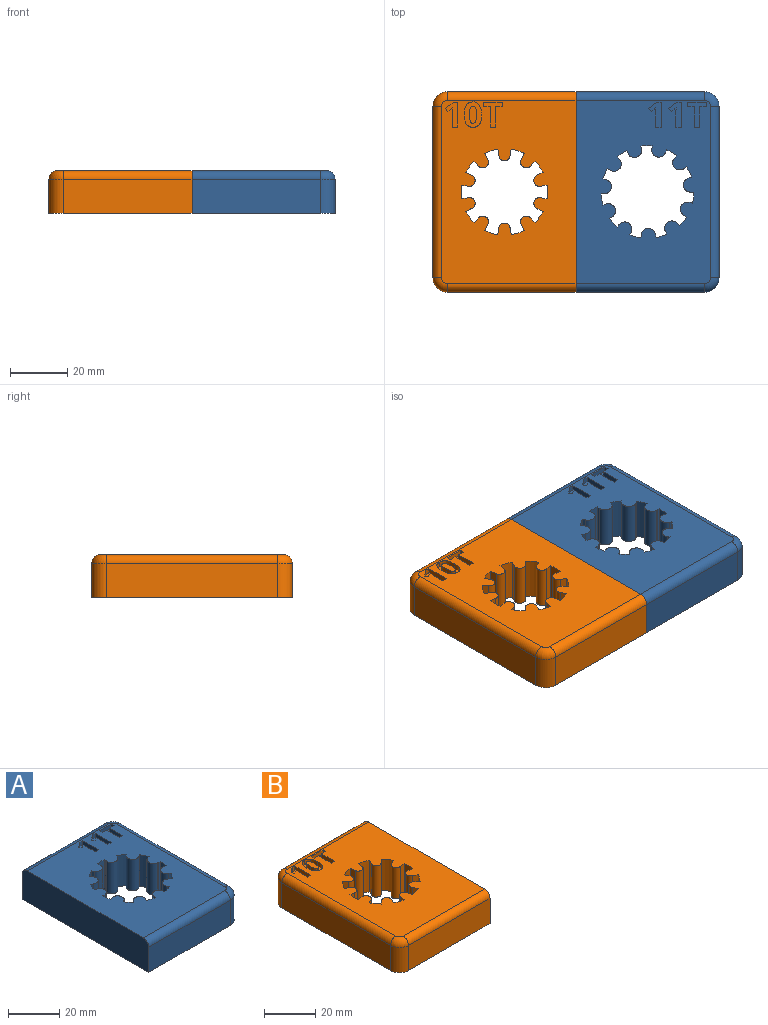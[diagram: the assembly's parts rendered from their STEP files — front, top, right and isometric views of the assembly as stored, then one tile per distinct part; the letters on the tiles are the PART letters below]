
ASSEMBLY  parts=2 mates=1
PART A: 101 faces, bbox 50x70x15 mm
  f0: plane 64x47mm, normal (0,0,1), area 2276.3mm2, adj f4,f6,f7,f8,f9,f10,f11,f12
  f1: plane 45x12mm, normal (0,-1,0), area 540mm2, adj f4,f5,f63,f69
  f2: plane 60x12mm, normal (1,0,0), area 720mm2, adj f5,f63,f64,f67
  f3: plane 45x12mm, normal (0,1,0), area 540mm2, adj f4,f5,f64,f65
  f4: plane 70x15mm, normal (-1,0,0), area 1046.1mm2, adj f0,f1,f3,f5,f65,f69
  f5: plane 70x50mm, normal (0,0,-1), area 2823.1mm2, adj f1,f2,f3,f4,f6,f7,f8,f9
  f6: cylinder r=16.23mm len=15mm, axis (0,0,1), area 59.6mm2, adj f0,f5,f7,f62
  f7: plane 15x0.99mm, normal (-0.99,0.12,0), area 15mm2, adj f0,f5,f6,f8
  f8: plane 15x0mm, normal (-0.1,-0.99,0), area 0.1mm2, adj f0,f5,f7,f9
  f9: plane 15x0.3mm, normal (-0.99,0.12,0), area 4.5mm2, adj f0,f5,f8,f10
  f10: cylinder r=2.5mm len=15mm, axis (0,0,1), area 102.6mm2, adj f0,f5,f9,f11
  f11: plane 15x1.2mm, normal (0.92,-0.4,0), area 19.5mm2, adj f0,f5,f10,f12
  f12: cylinder r=16.23mm len=15mm, axis (0,0,1), area 59.7mm2, adj f0,f5,f11,f13
  f13: plane 15x1mm, normal (-0.77,0.64,0), area 19.5mm2, adj f0,f5,f12,f14
  f14: cylinder r=2.5mm len=15mm, axis (0,0,1), area 102.6mm2, adj f0,f5,f13,f15
  f15: plane 15x1.08mm, normal (0.56,-0.83,0), area 19.5mm2, adj f0,f5,f14,f16
  f16: cylinder r=16.23mm len=15mm, axis (0,0,1), area 59.7mm2, adj f0,f5,f15,f17
  f17: plane 15x1.24mm, normal (-0.3,0.95,0), area 19.5mm2, adj f0,f5,f16,f18
  f18: cylinder r=2.5mm len=15mm, axis (0,0,1), area 102.5mm2, adj f0,f5,f17,f19
  f19: plane 15x0.31mm, normal (0.02,-1,0), area 4.6mm2, adj f0,f5,f18,f20
  f20: cylinder r=15.23mm len=15mm, axis (0,0,1), area 0.3mm2, adj f0,f5,f19,f21
  f21: plane 15x1mm, normal (0.02,-1,0), area 15mm2, adj f0,f5,f20,f22
  f22: cylinder r=16.23mm len=15mm, axis (0,0,1), area 59.3mm2, adj f0,f5,f21,f23
  f23: plane 15x1.26mm, normal (0.26,0.96,0), area 19.5mm2, adj f0,f5,f22,f24
  f24: cylinder r=2.5mm len=15mm, axis (0,0,1), area 107.1mm2, adj f0,f5,f23,f25
  f25: plane 15x0mm, normal (-0.84,0.54,0), area 0.1mm2, adj f0,f5,f24,f26
  f26: plane 15x0.85mm, normal (-0.52,-0.85,0), area 15mm2, adj f0,f5,f25,f27
  f27: cylinder r=16.23mm len=15mm, axis (0,0,1), area 59.5mm2, adj f0,f5,f26,f28
  f28: plane 15x0.74mm, normal (0.74,0.67,0), area 15mm2, adj f0,f5,f27,f29
  f29: plane 15x0mm, normal (-0.69,0.73,0), area 0.1mm2, adj f0,f5,f28,f30
  f30: cylinder r=2.5mm len=15mm, axis (0,0,1), area 111.6mm2, adj f0,f5,f29,f31
  f31: plane 15x0mm, normal (-0.41,0.91,0), area 0.1mm2, adj f0,f5,f30,f32
  f32: plane 15x0.9mm, normal (-0.9,-0.43,0), area 15mm2, adj f0,f5,f31,f33
  f33: cylinder r=16.23mm len=15mm, axis (0,0,1), area 59.5mm2, adj f0,f5,f32,f34
  f34: plane 15x0.99mm, normal (0.99,0.16,0), area 15mm2, adj f0,f5,f33,f35
  f35: plane 15x0mm, normal (-0.18,0.98,0), area 0.1mm2, adj f0,f5,f34,f36
  f36: cylinder r=2.5mm len=15mm, axis (0,0,1), area 107.1mm2, adj f0,f5,f35,f37
  f37: plane 15x1.29mm, normal (-0.99,0.12,0), area 19.5mm2, adj f0,f5,f36,f38
  f38: cylinder r=16.23mm len=15mm, axis (0,0,1), area 59.6mm2, adj f0,f5,f37,f39
  f39: plane 15x0.92mm, normal (0.92,-0.4,0), area 15mm2, adj f0,f5,f38,f40
  f40: plane 15x0mm, normal (0.38,0.93,0), area 0.1mm2, adj f0,f5,f39,f41
  f41: cylinder r=2.5mm len=15mm, axis (0,0,1), area 111.6mm2, adj f0,f5,f40,f42
  f42: plane 15x0mm, normal (0.66,0.75,0), area 0.1mm2, adj f0,f5,f41,f43
  f43: plane 15x0.77mm, normal (-0.77,0.64,0), area 15mm2, adj f0,f5,f42,f44
  f44: cylinder r=16.23mm len=15mm, axis (0,0,1), area 59.5mm2, adj f0,f5,f43,f45
  f45: plane 15x0.83mm, normal (0.56,-0.83,0), area 15mm2, adj f0,f5,f44,f46
  f46: plane 15x0mm, normal (0.82,0.58,0), area 0.1mm2, adj f0,f5,f45,f47
  f47: cylinder r=2.5mm len=15mm, axis (0,0,1), area 111.6mm2, adj f0,f5,f46,f48
  f48: plane 15x0mm, normal (0.96,0.28,0), area 0.1mm2, adj f0,f5,f47,f49
  f49: plane 15x0.95mm, normal (-0.3,0.95,0), area 15mm2, adj f0,f5,f48,f50
  f50: cylinder r=16.23mm len=15mm, axis (0,0,1), area 59.9mm2, adj f0,f5,f49,f51
  f51: plane 15x1.5mm, normal (0.02,-1,0), area 22.5mm2, adj f0,f5,f50,f52
  f52: cylinder r=2.5mm len=15mm, axis (0,0,1), area 104.2mm2, adj f0,f5,f51,f53
  f53: plane 15x0mm, normal (0.96,-0.28,0), area 0.1mm2, adj f0,f5,f52,f54
  f54: plane 15x0.97mm, normal (0.26,0.96,0), area 15mm2, adj f0,f5,f53,f55
  f55: cylinder r=16.23mm len=15mm, axis (0,0,1), area 59.6mm2, adj f0,f5,f54,f56
  f56: plane 15x1.11mm, normal (-0.52,-0.85,0), area 19.5mm2, adj f0,f5,f55,f57
  f57: cylinder r=2.5mm len=15mm, axis (0,0,1), area 102.6mm2, adj f0,f5,f56,f58
  f58: plane 15x0.97mm, normal (0.74,0.67,0), area 19.5mm2, adj f0,f5,f57,f59
  f59: cylinder r=16.23mm len=15mm, axis (0,0,1), area 59.7mm2, adj f0,f5,f58,f60
  f60: plane 15x1.17mm, normal (-0.9,-0.43,0), area 19.5mm2, adj f0,f5,f59,f61
  f61: cylinder r=2.5mm len=15mm, axis (0,0,1), area 102.6mm2, adj f0,f5,f60,f62
  f62: plane 15x1.29mm, normal (0.99,0.16,0), area 19.5mm2, adj f0,f5,f6,f61
  f63: cylinder r=5mm len=12mm, axis (0,0,1), area 94.2mm2, adj f1,f2,f5,f68
  f64: cylinder r=5mm len=12mm, axis (0,0,-1), area 94.2mm2, adj f2,f3,f5,f66
  f65: cylinder r=3mm len=45mm, axis (1,0,0), area 212.1mm2, adj f0,f3,f4,f66
  f66: torus R=2mm, axis (0,0,1), area 28.9mm2, adj f0,f64,f65,f67
  f67: cylinder r=3mm len=60mm, axis (0,-1,0), area 282.7mm2, adj f0,f2,f66,f68
  f68: torus R=2mm, axis (0,0,1), area 28.9mm2, adj f0,f63,f67,f69
  f69: cylinder r=3mm len=45mm, axis (-1,0,0), area 212.1mm2, adj f0,f1,f4,f68
  f70: plane 2x1.87mm, normal (0,1,0), area 3.7mm2, adj f0,f71,f77,f78
  f71: plane 7.24x2mm, normal (-1,0,0), area 14.5mm2, adj f0,f70,f72,f78
  f72: plane 2.39x2mm, normal (0,1,0), area 4.8mm2, adj f0,f71,f73,f78
  f73: plane 2x1.55mm, normal (-1,0,0), area 3.1mm2, adj f0,f72,f74,f78
  f74: plane 6.64x2mm, normal (0,-1,0), area 13.3mm2, adj f0,f73,f75,f78
  f75: plane 2x1.55mm, normal (1,0,0), area 3.1mm2, adj f0,f74,f76,f78
  f76: plane 2.39x2mm, normal (0,1,0), area 4.8mm2, adj f0,f75,f77,f78
  f77: plane 7.24x2mm, normal (1,0,0), area 14.5mm2, adj f0,f70,f76,f78
  f78: plane 8.79x6.64mm, normal (0,0,1), area 23.8mm2, adj f70,f71,f72,f73,f74,f75,f76,f77
  f79: plane 2x1.86mm, normal (0,1,0), area 3.7mm2, adj f0,f80,f88,f89
  f80: plane 8.79x2mm, normal (-1,0,0), area 17.6mm2, adj f0,f79,f81,f89
  f81: plane 2x1.53mm, normal (0,-1,0), area 3.1mm2, adj f0,f80,f82,f89
  f82: plane 2.83x2.26mm, normal (0.62,-0.78,0), area 7.2mm2, adj f0,f81,f83,f89
  f83: plane 2x1.12mm, normal (0.78,0.63,0), area 2.9mm2, adj f0,f82,f84,f89
  f84: plane 2x1.01mm, normal (-0.63,0.78,0), area 2.6mm2, adj f0,f83,f85,f89
  f85: extruded ~2x0.64mm, area 1.8mm2, adj f0,f84,f86,f89
  f86: plane 2x0.91mm, normal (1,-0.03,0), area 1.8mm2, adj f0,f85,f87,f89
  f87: plane 2x0.84mm, normal (1,-0.02,0), area 1.7mm2, adj f0,f86,f88,f89
  f88: plane 5.09x2mm, normal (1,0,0), area 10.2mm2, adj f0,f79,f87,f89
  f89: plane 8.79x4.36mm, normal (0,0,1), area 20mm2, adj f79,f80,f81,f82,f83,f84,f85,f86
  f90: plane 2x1.86mm, normal (0,1,0), area 3.7mm2, adj f0,f91,f99,f100
  f91: plane 8.79x2mm, normal (-1,0,0), area 17.6mm2, adj f0,f90,f92,f100
  f92: plane 2x1.53mm, normal (0,-1,0), area 3.1mm2, adj f0,f91,f93,f100
  f93: plane 2.83x2.26mm, normal (0.62,-0.78,0), area 7.2mm2, adj f0,f92,f94,f100
  f94: plane 2x1.12mm, normal (0.78,0.63,0), area 2.9mm2, adj f0,f93,f95,f100
  f95: plane 2x1.01mm, normal (-0.63,0.78,0), area 2.6mm2, adj f0,f94,f96,f100
  f96: extruded ~2x0.64mm, area 1.8mm2, adj f0,f95,f97,f100
  f97: plane 2x0.91mm, normal (1,-0.03,0), area 1.8mm2, adj f0,f96,f98,f100
  f98: plane 2x0.84mm, normal (1,-0.02,0), area 1.7mm2, adj f0,f97,f99,f100
  f99: plane 5.09x2mm, normal (1,0,0), area 10.2mm2, adj f0,f90,f98,f100
  f100: plane 8.79x4.36mm, normal (0,0,1), area 20mm2, adj f90,f91,f92,f93,f94,f95,f96,f97
PART B: 91 faces, bbox 50x70x15 mm
  f0: plane 64x47mm, normal (0,0,1), area 2357.6mm2, adj f2,f6,f7,f8,f9,f10,f11,f12
  f1: plane 45x12mm, normal (0,-1,0), area 540mm2, adj f2,f5,f47,f52
  f2: plane 70x15mm, normal (1,0,0), area 1046.1mm2, adj f0,f1,f3,f5,f48,f52
  f3: plane 45x12mm, normal (0,1,0), area 540mm2, adj f2,f5,f46,f48
  f4: plane 60x12mm, normal (-1,0,0), area 720mm2, adj f5,f46,f47,f50
  f5: plane 70x50mm, normal (0,0,-1), area 2928.1mm2, adj f1,f2,f3,f4,f6,f7,f8,f9
  f6: plane 15x2.16mm, normal (-0.45,0.89,0), area 36.4mm2, adj f0,f5,f7,f45
  f7: cylinder r=15.12mm len=15mm, axis (0,0,1), area 71.6mm2, adj f0,f5,f6,f8
  f8: plane 15x1.68mm, normal (0.71,-0.71,0), area 35.7mm2, adj f0,f5,f7,f9
  f9: cylinder r=2mm len=15mm, axis (0,0,1), area 84.9mm2, adj f0,f5,f8,f10
  f10: plane 15x2.12mm, normal (-0.89,0.46,0), area 35.7mm2, adj f0,f5,f9,f11
  f11: cylinder r=15.12mm len=15mm, axis (0,0,1), area 72.7mm2, adj f0,f5,f10,f12
  f12: plane 15x2.66mm, normal (0.99,-0.15,0), area 40.3mm2, adj f0,f5,f11,f13
  f13: cylinder r=2mm len=15mm, axis (0,0,1), area 75.7mm2, adj f0,f5,f12,f14
  f14: plane 15x2.66mm, normal (-0.99,-0.15,0), area 40.3mm2, adj f0,f5,f13,f15
  f15: cylinder r=15.12mm len=15mm, axis (0,0,1), area 73mm2, adj f0,f5,f14,f16
  f16: plane 15x2.48mm, normal (0.89,0.46,0), area 41.7mm2, adj f0,f5,f15,f17
  f17: cylinder r=2mm len=15mm, axis (0,0,1), area 78.9mm2, adj f0,f5,f16,f18
  f18: plane 15x1.69mm, normal (-0.71,-0.71,0), area 35.7mm2, adj f0,f5,f17,f19
  f19: cylinder r=15.12mm len=15mm, axis (0,0,1), area 71.9mm2, adj f0,f5,f18,f20
  f20: plane 15x2.12mm, normal (0.45,0.89,0), area 35.7mm2, adj f0,f5,f19,f21
  f21: cylinder r=2mm len=15mm, axis (0,0,1), area 84.9mm2, adj f0,f5,f20,f22
  f22: plane 15x2.35mm, normal (-0.16,-0.99,0), area 35.7mm2, adj f0,f5,f21,f23
  f23: cylinder r=15.12mm len=15mm, axis (0,0,1), area 71.9mm2, adj f0,f5,f22,f24
  f24: plane 15x2.35mm, normal (-0.16,0.99,0), area 35.7mm2, adj f0,f5,f23,f25
  f25: cylinder r=2mm len=15mm, axis (0,0,1), area 84.9mm2, adj f0,f5,f24,f26
  f26: plane 15x2.12mm, normal (0.45,-0.89,0), area 35.7mm2, adj f0,f5,f25,f27
  f27: cylinder r=15.12mm len=15mm, axis (0,0,1), area 72.6mm2, adj f0,f5,f26,f28
  f28: plane 15x1.69mm, normal (-0.71,0.7,0), area 35.7mm2, adj f0,f5,f27,f29
  f29: cylinder r=2mm len=15mm, axis (0,0,1), area 84.9mm2, adj f0,f5,f28,f30
  f30: plane 15x2.12mm, normal (0.89,-0.45,0), area 35.7mm2, adj f0,f5,f29,f31
  f31: cylinder r=15.12mm len=15mm, axis (0,0,1), area 71.3mm2, adj f0,f5,f30,f32
  f32: plane 15x2.35mm, normal (-0.99,0.15,0), area 35.7mm2, adj f0,f5,f31,f33
  f33: cylinder r=2mm len=15mm, axis (0,0,1), area 85mm2, adj f0,f5,f32,f34
  f34: plane 15x2.35mm, normal (0.99,0.15,0), area 35.7mm2, adj f0,f5,f33,f35
  f35: cylinder r=15.12mm len=15mm, axis (0,0,1), area 72mm2, adj f0,f5,f34,f36
  f36: plane 15x2.12mm, normal (-0.89,-0.46,0), area 35.7mm2, adj f0,f5,f35,f37
  f37: cylinder r=2mm len=15mm, axis (0,0,1), area 85mm2, adj f0,f5,f36,f38
  f38: plane 15x1.69mm, normal (0.71,0.71,0), area 35.7mm2, adj f0,f5,f37,f39
  f39: cylinder r=15.12mm len=15mm, axis (0,0,1), area 71.9mm2, adj f0,f5,f38,f40
  f40: plane 15x2.12mm, normal (-0.45,-0.89,0), area 35.7mm2, adj f0,f5,f39,f41
  f41: cylinder r=2mm len=15mm, axis (0,0,1), area 84.9mm2, adj f0,f5,f40,f42
  f42: plane 15x2.35mm, normal (0.16,0.99,0), area 35.7mm2, adj f0,f5,f41,f43
  f43: cylinder r=15.12mm len=15mm, axis (0,0,1), area 71.9mm2, adj f0,f5,f42,f44
  f44: plane 15x2.35mm, normal (0.16,-0.99,0), area 35.7mm2, adj f0,f5,f43,f45
  f45: cylinder r=2mm len=15mm, axis (0,0,1), area 84.2mm2, adj f0,f5,f6,f44
  f46: cylinder r=5mm len=12mm, axis (0,0,1), area 94.2mm2, adj f3,f4,f5,f49
  f47: cylinder r=5mm len=12mm, axis (0,0,-1), area 94.2mm2, adj f1,f4,f5,f51
  f48: cylinder r=3mm len=45mm, axis (1,0,0), area 212.1mm2, adj f0,f2,f3,f49
  f49: torus R=2mm, axis (0,0,1), area 28.9mm2, adj f0,f46,f48,f50
  f50: cylinder r=3mm len=60mm, axis (0,1,0), area 282.7mm2, adj f0,f4,f49,f51
  f51: torus R=2mm, axis (0,0,1), area 28.9mm2, adj f0,f47,f50,f52
  f52: cylinder r=3mm len=45mm, axis (-1,0,0), area 212.1mm2, adj f0,f1,f2,f51
  f53: extruded ~2.28x2mm, area 4.6mm2, adj f54,f68,f69,f90
  f54: extruded ~2.29x2mm, area 4.6mm2, adj f53,f55,f69,f90
  f55: extruded ~2x0.92mm, area 2.5mm2, adj f54,f56,f69,f90
  f56: extruded ~2x0.92mm, area 2.5mm2, adj f55,f57,f69,f90
  f57: extruded ~2.29x2mm, area 4.6mm2, adj f56,f58,f69,f90
  f58: extruded ~2.27x2mm, area 4.6mm2, adj f57,f59,f69,f90
  f59: extruded ~2x0.93mm, area 2.5mm2, adj f58,f68,f69,f90
  f60: extruded ~3.36x2mm, area 7mm2, adj f0,f61,f67,f69
  f61: extruded ~3.33x2mm, area 6.9mm2, adj f0,f60,f62,f69
  f62: extruded ~2.27x2mm, area 5.3mm2, adj f0,f61,f63,f69
  f63: extruded ~2.28x2mm, area 5.3mm2, adj f0,f62,f64,f69
  f64: extruded ~3.38x2mm, area 7mm2, adj f0,f63,f65,f69
  f65: extruded ~3.32x2mm, area 6.9mm2, adj f0,f64,f66,f69
  f66: extruded ~2.26x2mm, area 5.3mm2, adj f0,f65,f67,f69
  f67: extruded ~2.29x2mm, area 5.3mm2, adj f0,f60,f66,f69
  f68: extruded ~2x0.93mm, area 2.5mm2, adj f53,f59,f69,f90
  f69: plane 8.92x6.05mm, normal (0,0,1), area 32.8mm2, adj f53,f54,f55,f56,f57,f58,f59,f60
  f70: plane 2x1.84mm, normal (0,1,0), area 3.7mm2, adj f0,f71,f77,f78
  f71: plane 7.13x2mm, normal (-1,0,0), area 14.3mm2, adj f0,f70,f72,f78
  f72: plane 2.35x2mm, normal (0,1,0), area 4.7mm2, adj f0,f71,f73,f78
  f73: plane 2x1.53mm, normal (-1,0,0), area 3.1mm2, adj f0,f72,f74,f78
  f74: plane 6.54x2mm, normal (0,-1,0), area 13.1mm2, adj f0,f73,f75,f78
  f75: plane 2x1.53mm, normal (1,0,0), area 3.1mm2, adj f0,f74,f76,f78
  f76: plane 2.35x2mm, normal (0,1,0), area 4.7mm2, adj f0,f75,f77,f78
  f77: plane 7.13x2mm, normal (1,0,0), area 14.3mm2, adj f0,f70,f76,f78
  f78: plane 8.66x6.54mm, normal (0,0,1), area 23.1mm2, adj f70,f71,f72,f73,f74,f75,f76,f77
  f79: plane 2x1.83mm, normal (0,1,0), area 3.7mm2, adj f0,f80,f88,f89
  f80: plane 8.66x2mm, normal (-1,0,0), area 17.3mm2, adj f0,f79,f81,f89
  f81: plane 2x1.51mm, normal (0,-1,0), area 3mm2, adj f0,f80,f82,f89
  f82: plane 2.79x2.22mm, normal (0.62,-0.78,0), area 7.1mm2, adj f0,f81,f83,f89
  f83: plane 2x1.1mm, normal (0.78,0.63,0), area 2.8mm2, adj f0,f82,f84,f89
  f84: plane 2x1mm, normal (-0.63,0.78,0), area 2.6mm2, adj f0,f83,f85,f89
  f85: extruded ~2x0.63mm, area 1.7mm2, adj f0,f84,f86,f89
  f86: plane 2x0.9mm, normal (1,-0.03,0), area 1.8mm2, adj f0,f85,f87,f89
  f87: plane 2x0.82mm, normal (1,-0.02,0), area 1.6mm2, adj f0,f86,f88,f89
  f88: plane 5.01x2mm, normal (1,0,0), area 10mm2, adj f0,f79,f87,f89
  f89: plane 8.66x4.29mm, normal (0,0,1), area 19.4mm2, adj f79,f80,f81,f82,f83,f84,f85,f86
  f90: plane 5.96x2.41mm, normal (0,0,1), area 12.2mm2, adj f53,f54,f55,f56,f57,f58,f59,f68
PLACE A t=(46.11,23.69,-11.89)mm
PLACE B t=(-3.89,23.69,-11.89)mm
MATE parallel B.f2 <-> A.f4  axis (1,0,0) through (21.11,23.69,-4.42)mm
